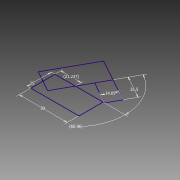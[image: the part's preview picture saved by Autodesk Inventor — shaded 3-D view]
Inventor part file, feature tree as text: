
AUTODESK INVENTOR PART (.ipt)
format: ipt  version: 2013 (Build 170138000, 138)  size: 67,072 bytes
history: native  units: mm
features: sketch x1
ambient origin geometry x8: Origin, YZ Plane, XZ Plane, XY Plane, X Axis, Y Axis, Z Axis, Center Point
feature tree (1):
  sketch  "Sketch1"  dims[d0=25.0mm d3=14.05mm d4=10.639717mm d5=50.0mm d6=21.237276mm d8=26.5mm]
